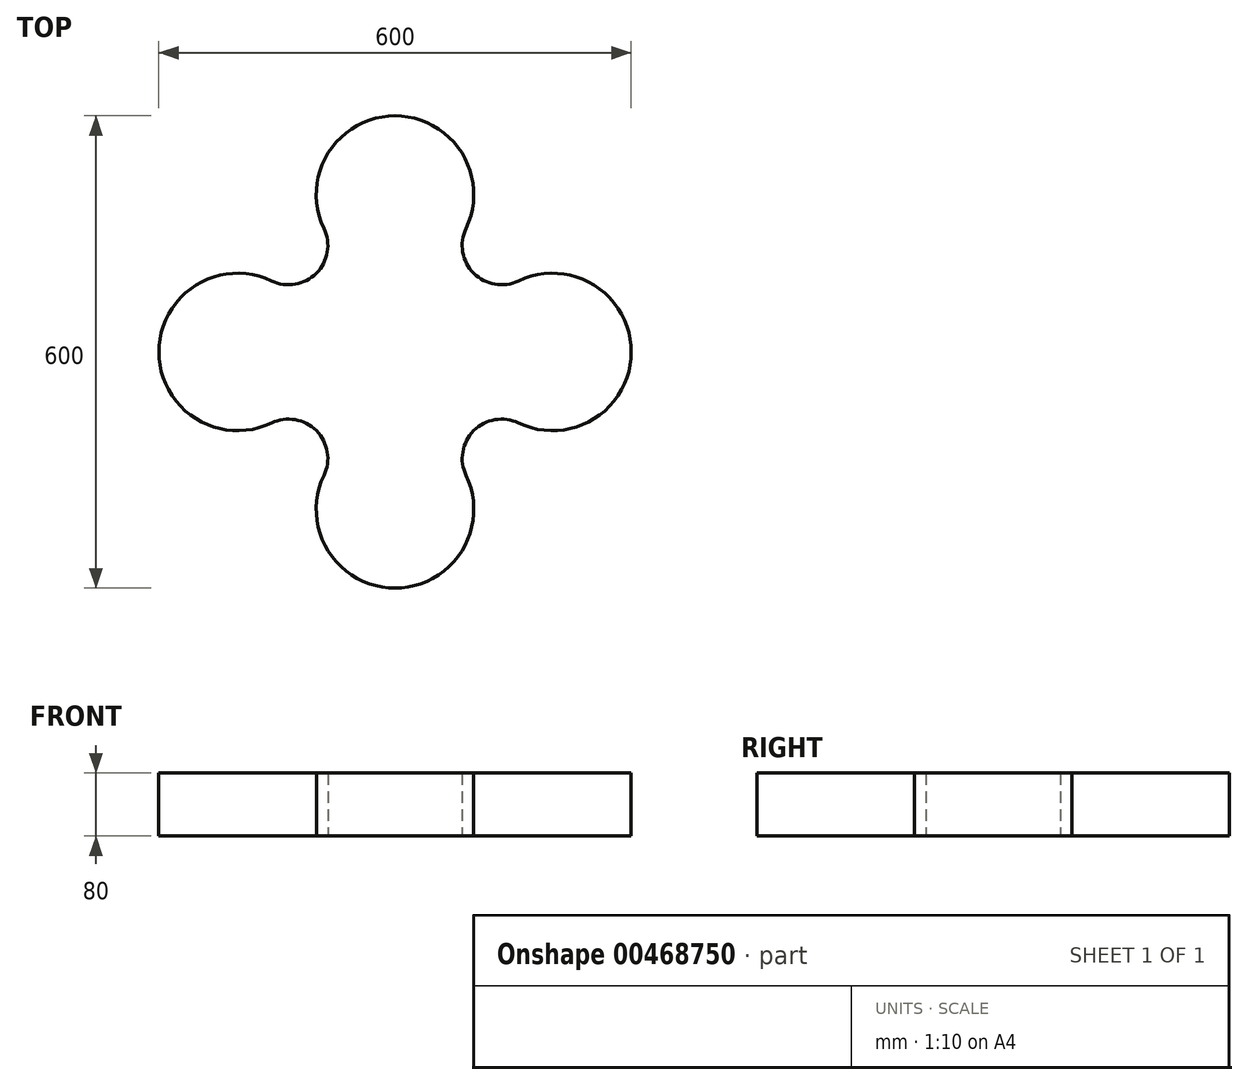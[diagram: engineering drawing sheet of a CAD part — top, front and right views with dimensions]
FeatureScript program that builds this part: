
annotation { "Feature Type Name" : "Feature", "Feature Type Description" : "" }
export const myFeature = defineFeature(function(context is Context, id is Id, definition is map)
    precondition{}
    {
        {
            var Q0;
            Q0=qCreatedBy(makeId("Top.planeOp"),FACE);
            var sketch = newSketch(context, id + "F0", { "sketchPlane" : qUnion([Q0])});
            skLineSegment(sketch, "E0.bottom", {"start": v(100, -100) * mm, "end": v(-100, -100) * mm});
            skLineSegment(sketch, "E0.top", {"start": v(100, 100) * mm, "end": v(-100, 100) * mm});
            skLineSegment(sketch, "E0.left", {"start": v(100, -100) * mm, "end": v(100, 100) * mm});
            skLineSegment(sketch, "E0.right", {"start": v(-100, -100) * mm, "end": v(-100, 100) * mm});
            skPoint(sketch, "E0.middle", {"position": v(0, 0) * mm});
            skLineSegment(sketch, "E1.0", {"start": v(300, 300) * mm, "end": v(-300, 300) * mm});
            skLineSegment(sketch, "E1.1", {"start": v(300, -300) * mm, "end": v(300, 300) * mm});
            skLineSegment(sketch, "E1.2", {"start": v(300, -300) * mm, "end": v(-300, -300) * mm});
            skLineSegment(sketch, "E1.3", {"start": v(-300, -300) * mm, "end": v(-300, 300) * mm});
            skCircle(sketch, "E2", {"center": v(-200, 0) * mm, "radius": 100 * mm});
            skPoint(sketch, "E2.centerSnap0", {"position": v(-100, 0) * mm});
            skCircle(sketch, "E3", {"center": v(200, 0) * mm, "radius": 100 * mm});
            skCircle(sketch, "E4", {"center": v(0, 200) * mm, "radius": 100 * mm});
            skCircle(sketch, "E5", {"center": v(0, -200) * mm, "radius": 100 * mm});
            skArc(sketch, "E6", {"start": v(-156.9, 90.24) * mm, "mid": v(-100, 100) * mm, "end": v(-90.24, 156.9) * mm});
            skArc(sketch, "E7", {"start": v(90.24, 156.9) * mm, "mid": v(100, 100) * mm, "end": v(156.9, 90.24) * mm});
            skArc(sketch, "E8", {"start": v(-90.24, -156.9) * mm, "mid": v(-100, -100) * mm, "end": v(-156.9, -90.24) * mm});
            skArc(sketch, "E9", {"start": v(156.9, -90.24) * mm, "mid": v(100, -100) * mm, "end": v(90.24, -156.9) * mm});
            skSolve(sketch);
        }
        {
            var Q0;
            {var subQ0=sQuery(id+"F0.wireOp",EDGE,"E2");var subQ1=makeQuery(id+"F0.imprint","INTERSECT",VERTEX,{"derivedFrom":[subQ0,sQuery(id+"F0.wireOp",EDGE,"E6")]});Q0=makeQuery(id+"F0.imprint","IMPRINT",FACE,{"disambiguationData":[TD([[makeQuery(id+"F0.imprint","IMPRINT",EDGE,{"disambiguationData":[TD([[subQ1,1.0]])],"derivedFrom":subQ0}),1.0]])]});}
            var Q1;
            {var subQ0=sQuery(id+"F0.wireOp",EDGE,"E4");var subQ1=makeQuery(id+"F0.imprint","INTERSECT",VERTEX,{"derivedFrom":[subQ0,sQuery(id+"F0.wireOp",EDGE,"E6")]});Q1=makeQuery(id+"F0.imprint","IMPRINT",FACE,{"disambiguationData":[TD([[makeQuery(id+"F0.imprint","IMPRINT",EDGE,{"disambiguationData":[TD([[subQ1,1.0]])],"derivedFrom":subQ0}),1.0]])]});}
            var Q2;
            {var subQ0=sQuery(id+"F0.wireOp",EDGE,"E3");var subQ1=makeQuery(id+"F0.imprint","INTERSECT",VERTEX,{"derivedFrom":[subQ0,sQuery(id+"F0.wireOp",EDGE,"E7")]});Q2=makeQuery(id+"F0.imprint","IMPRINT",FACE,{"disambiguationData":[TD([[makeQuery(id+"F0.imprint","IMPRINT",EDGE,{"disambiguationData":[TD([[subQ1,1.0]])],"derivedFrom":subQ0}),1.0]])]});}
            var Q3;
            {var subQ0=sQuery(id+"F0.wireOp",EDGE,"E5");var subQ1=makeQuery(id+"F0.imprint","INTERSECT",VERTEX,{"derivedFrom":[subQ0,sQuery(id+"F0.wireOp",EDGE,"E9")]});Q3=makeQuery(id+"F0.imprint","IMPRINT",FACE,{"disambiguationData":[TD([[makeQuery(id+"F0.imprint","IMPRINT",EDGE,{"disambiguationData":[TD([[subQ1,-1.0]])],"derivedFrom":subQ0}),1.0]])]});}
            var Q4;
            {var subQ0=sQuery(id+"F0.wireOp",EDGE,"E8");var subQ3=sQuery(id+"F0.wireOp",EDGE,"E5");var subQ5=makeQuery(id+"F0.imprint","INTERSECT",VERTEX,{"derivedFrom":[subQ3,subQ0]});Q4=makeQuery(id+"F0.imprint","IMPRINT",FACE,{"disambiguationData":[TD([[makeQuery(id+"F0.imprint","IMPRINT",EDGE,{"disambiguationData":[TD([[subQ5,1.0]])],"derivedFrom":subQ3}),-1.0]])]});}
            var Q5;
            {var subQ0=sQuery(id+"F0.wireOp",EDGE,"E8");var subQ3=sQuery(id+"F0.wireOp",EDGE,"E2");var subQ5=makeQuery(id+"F0.imprint","INTERSECT",VERTEX,{"derivedFrom":[subQ3,subQ0]});Q5=makeQuery(id+"F0.imprint","IMPRINT",FACE,{"disambiguationData":[TD([[makeQuery(id+"F0.imprint","IMPRINT",EDGE,{"disambiguationData":[TD([[subQ5,-1.0]])],"derivedFrom":subQ3}),-1.0]])]});}
            var Q6;
            {var subQ0=sQuery(id+"F0.wireOp",EDGE,"E6");var subQ3=sQuery(id+"F0.wireOp",EDGE,"E2");var subQ5=makeQuery(id+"F0.imprint","INTERSECT",VERTEX,{"derivedFrom":[subQ3,subQ0]});Q6=makeQuery(id+"F0.imprint","IMPRINT",FACE,{"disambiguationData":[TD([[makeQuery(id+"F0.imprint","IMPRINT",EDGE,{"disambiguationData":[TD([[subQ5,1.0]])],"derivedFrom":subQ3}),-1.0]])]});}
            var Q7;
            {var subQ0=sQuery(id+"F0.wireOp",EDGE,"E6");var subQ3=sQuery(id+"F0.wireOp",EDGE,"E4");var subQ5=makeQuery(id+"F0.imprint","INTERSECT",VERTEX,{"derivedFrom":[subQ3,subQ0]});Q7=makeQuery(id+"F0.imprint","IMPRINT",FACE,{"disambiguationData":[TD([[makeQuery(id+"F0.imprint","IMPRINT",EDGE,{"disambiguationData":[TD([[subQ5,-1.0]])],"derivedFrom":subQ3}),-1.0]])]});}
            var Q8;
            {var subQ0=sQuery(id+"F0.wireOp",EDGE,"E7");var subQ3=sQuery(id+"F0.wireOp",EDGE,"E4");var subQ5=makeQuery(id+"F0.imprint","INTERSECT",VERTEX,{"derivedFrom":[subQ3,subQ0]});Q8=makeQuery(id+"F0.imprint","IMPRINT",FACE,{"disambiguationData":[TD([[makeQuery(id+"F0.imprint","IMPRINT",EDGE,{"disambiguationData":[TD([[subQ5,1.0]])],"derivedFrom":subQ3}),-1.0]])]});}
            var Q9;
            {var subQ0=sQuery(id+"F0.wireOp",EDGE,"E7");var subQ3=sQuery(id+"F0.wireOp",EDGE,"E3");var subQ5=makeQuery(id+"F0.imprint","INTERSECT",VERTEX,{"derivedFrom":[subQ3,subQ0]});Q9=makeQuery(id+"F0.imprint","IMPRINT",FACE,{"disambiguationData":[TD([[makeQuery(id+"F0.imprint","IMPRINT",EDGE,{"disambiguationData":[TD([[subQ5,-1.0]])],"derivedFrom":subQ3}),-1.0]])]});}
            var Q10;
            {var subQ0=sQuery(id+"F0.wireOp",EDGE,"E9");var subQ3=sQuery(id+"F0.wireOp",EDGE,"E3");var subQ5=makeQuery(id+"F0.imprint","INTERSECT",VERTEX,{"derivedFrom":[subQ3,subQ0]});Q10=makeQuery(id+"F0.imprint","IMPRINT",FACE,{"disambiguationData":[TD([[makeQuery(id+"F0.imprint","IMPRINT",EDGE,{"disambiguationData":[TD([[subQ5,1.0]])],"derivedFrom":subQ3}),-1.0]])]});}
            var Q11;
            {var subQ6=sQuery(id+"F0.wireOp",EDGE,"E0.bottom");var subQ8=makeQuery(id+"F0.imprint","INTERSECT",VERTEX,{"derivedFrom":[subQ6,sQuery(id+"F0.wireOp",EDGE,"E5")]});Q11=makeQuery(id+"F0.imprint","IMPRINT",FACE,{"disambiguationData":[TD([[makeQuery(id+"F0.imprint","IMPRINT",EDGE,{"disambiguationData":[TD([[subQ8,1.0]])],"derivedFrom":subQ6}),-1.0]])]});}
            var Q12;
            {var subQ0=sQuery(id+"F0.wireOp",EDGE,"E9");var subQ3=sQuery(id+"F0.wireOp",EDGE,"E5");var subQ5=makeQuery(id+"F0.imprint","INTERSECT",VERTEX,{"derivedFrom":[subQ3,subQ0]});Q12=makeQuery(id+"F0.imprint","IMPRINT",FACE,{"disambiguationData":[TD([[makeQuery(id+"F0.imprint","IMPRINT",EDGE,{"disambiguationData":[TD([[subQ5,-1.0]])],"derivedFrom":subQ3}),-1.0]])]});}
            extrude(context, id + "F1", {"entities" : qUnion([Q0, Q1, Q2, Q3, Q4, Q5, Q6, Q7, Q8, Q9, Q10, Q11, Q12]), "depth" : 80 * mm});
        }
    });
